FCSTD DOCUMENT  (FreeCAD 0.16R6710 (Git))
Label: Mega2560
License: All rights reserved
LicenseURL: http://en.wikipedia.org/wiki/All_rights_reserved
objects: Sketcher::SketchObject×1
note: 1 computed .brp shape members not serialized (recipe doc carries the construction recipe); baked Part::Feature solids carry a one-line shape summary decoded from their .brp

FEATURE [Sketcher::SketchObject] Sketch
  Placement = pos=(300,110,0) rot=(0,0,1;0rad)
  sketch-geometry (10):
    g0: LineSegment StartX=0 StartY=53.3 StartZ=0 EndX=101.6 EndY=53.3 EndZ=0
    g1: LineSegment StartX=101.6 StartY=53.3 StartZ=0 EndX=101.6 EndY=0 EndZ=0
    g2: LineSegment StartX=101.6 StartY=0 StartZ=0 EndX=0 EndY=0 EndZ=0
    g3: LineSegment StartX=0 StartY=0 StartZ=0 EndX=0 EndY=53.3 EndZ=0
    g4: Circle CenterX=15.3 CenterY=50.8 CenterZ=0 NormalX=0 NormalY=0 NormalZ=1 Radius=1.6
    g5: Circle CenterX=13.9 CenterY=2.5 CenterZ=0 NormalX=0 NormalY=0 NormalZ=1 Radius=1.6
    g6: Circle CenterX=66.1 CenterY=35.6 CenterZ=0 NormalX=0 NormalY=0 NormalZ=1 Radius=1.6
    g7: Circle CenterX=66.1 CenterY=7.7 CenterZ=0 NormalX=0 NormalY=0 NormalZ=1 Radius=1.6
    g8: Circle CenterX=96.52 CenterY=2.6 CenterZ=0 NormalX=0 NormalY=0 NormalZ=1 Radius=1.6
    g9: Circle CenterX=90.2 CenterY=50.8 CenterZ=0 NormalX=0 NormalY=0 NormalZ=1 Radius=1.6
  constraints (29):
    c: Coincident(g0,g1)
    c: Coincident(g1,g2)
    c: Coincident(g2,g3)
    c: Coincident(g3,g0)
    c: Horizontal(g0)
    c: Horizontal(g2)
    c: Vertical(g1)
    c: Vertical(g3)
    c: Radius(g4) = 1.6
    c: DistanceX(g0,g4) = 15.3
    c: DistanceY(g4,g0) = 2.5
    c: DistanceX(g0,g0) = 101.6
    c: DistanceY(g2,g5) = 2.5
    c: DistanceX(g5,g4) = 1.4
    c: DistanceX(g4,g6) = 50.8
    c: DistanceY(g6,g4) = 15.2
    c: DistanceX(g7,g6) = 0
    c: DistanceY(g7,g6) = 27.9
    c: Equal(g4,g9)
    c: Equal(g9,g6)
    c: Equal(g6,g7)
    c: Equal(g7,g8)
    c: Equal(g8,g5)
    c: DistanceY(g1,g1) = 53.3
    c: DistanceX(g6,g9) = 24.1
    c: DistanceY(g8,g7) = 5.1
    c: Coincident(g2,g-1)
    c: DistanceY(g9,g4) = 0
    c: DistanceX(g-1,g8) = 96.52
